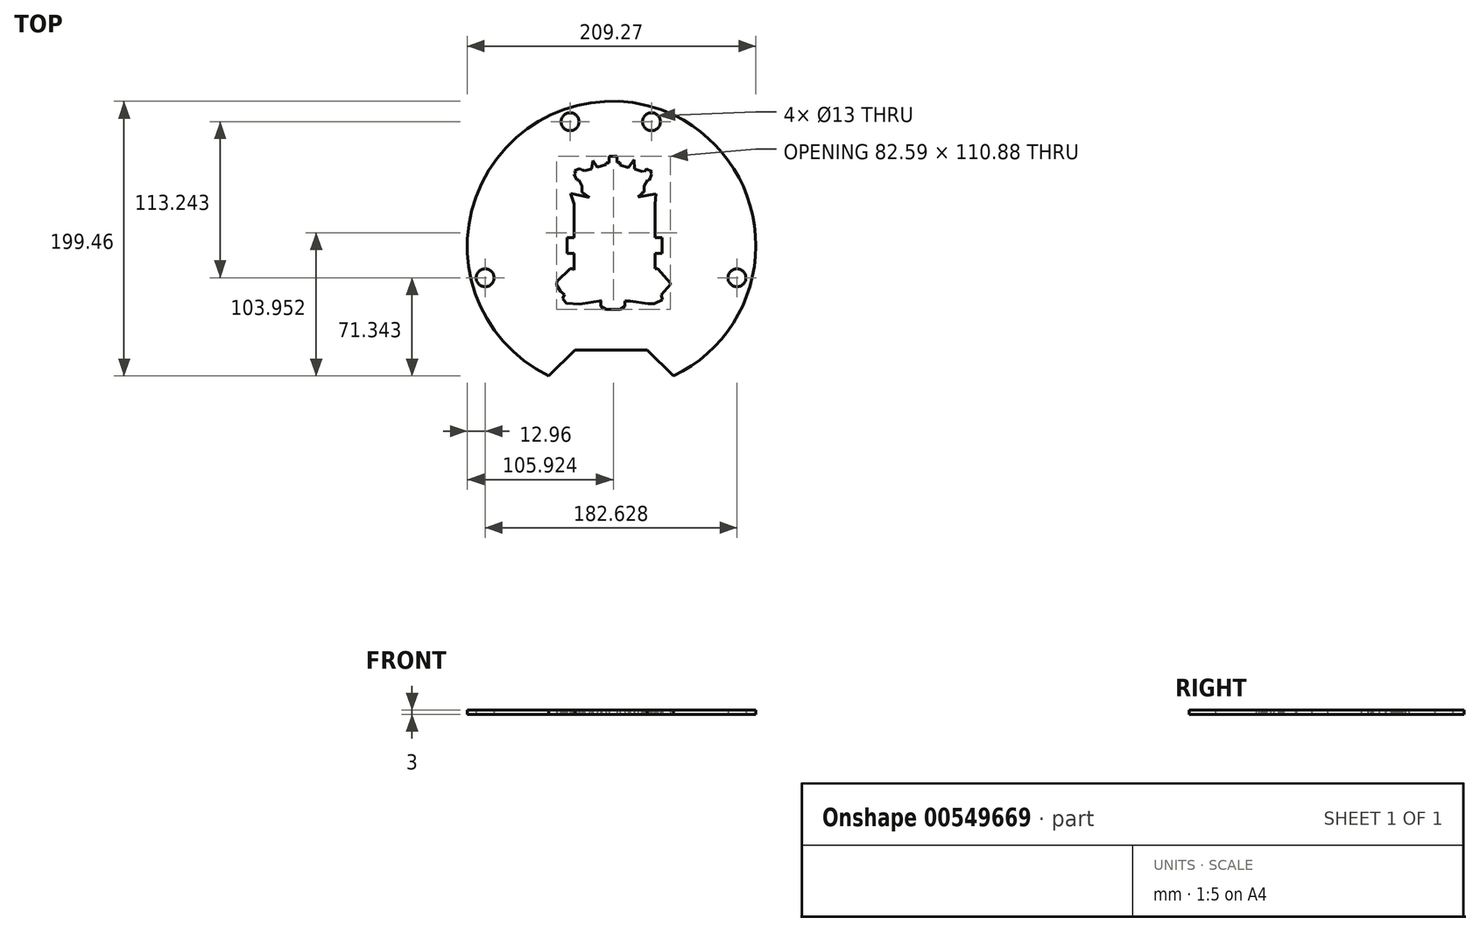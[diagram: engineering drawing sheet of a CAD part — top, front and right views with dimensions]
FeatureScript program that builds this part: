
annotation { "Feature Type Name" : "Feature", "Feature Type Description" : "" }
export const myFeature = defineFeature(function(context is Context, id is Id, definition is map)
    precondition{}
    {
        {
            var Q0;
            Q0=qCreatedBy(makeId("Top.planeOp"),FACE);
            var sketch = newSketch(context, id + "F0", { "sketchPlane" : qUnion([Q0])});
            skCircle(sketch, "E0", {"center": v(0, 0) * mm, "radius": 105 * mm});
            skLineSegment(sketch, "E1", {"start": v(0, 105) * mm, "end": v(0, -105) * mm});
            skLineSegment(sketch, "E2", {"start": v(0, 0) * mm, "end": v(0, 105) * mm});
            skLineSegment(sketch, "E3", {"start": v(-23.84, -72.43) * mm, "end": v(-45.86, -94.46) * mm});
            skLineSegment(sketch, "E4", {"start": v(22.77, -72.43) * mm, "end": v(45.13, -94.8) * mm});
            skPoint(sketch, "E5.firstSnap0", {"position": v(0, 46.64) * mm});
            skLineSegment(sketch, "E6", {"start": v(-21.81, 43.54) * mm, "end": v(-21.81, 39.03) * mm});
            skLineSegment(sketch, "E7", {"start": v(-21.81, 39.03) * mm, "end": v(-16.4, 35.15) * mm});
            skLineSegment(sketch, "E8", {"start": v(-16.4, 35.15) * mm, "end": v(-30.05, 38.05) * mm});
            skLineSegment(sketch, "E9", {"start": v(-30.05, 38.05) * mm, "end": v(-27.5, 30.4) * mm});
            skLineSegment(sketch, "E10", {"start": v(-27.5, 30.4) * mm, "end": v(-27.5, -17.4) * mm});
            skLineSegment(sketch, "E11", {"start": v(-27.5, -17.4) * mm, "end": v(-28.68, -16.54) * mm});
            skLineSegment(sketch, "E12", {"start": v(-28.68, -16.54) * mm, "end": v(-30.4, -16.54) * mm});
            skLineSegment(sketch, "E13", {"start": v(-30.4, -16.54) * mm, "end": v(-39.76, -25.66) * mm});
            skLineSegment(sketch, "E14", {"start": v(-39.76, -25.66) * mm, "end": v(-40.37, -28.38) * mm});
            skLineSegment(sketch, "E15", {"start": v(-40.37, -28.38) * mm, "end": v(-37.5, -32.94) * mm});
            skLineSegment(sketch, "E16", {"start": v(-37.5, -32.94) * mm, "end": v(-34.59, -35.38) * mm});
            skLineSegment(sketch, "E17", {"start": v(-34.59, -35.38) * mm, "end": v(-35.9, -38.1) * mm});
            skLineSegment(sketch, "E18", {"start": v(-35.9, -38.1) * mm, "end": v(-33.17, -41.48) * mm});
            skLineSegment(sketch, "E19", {"start": v(-33.17, -41.48) * mm, "end": v(-23.33, -42.39) * mm});
            skLineSegment(sketch, "E20", {"start": v(-23.33, -42.39) * mm, "end": v(-7.42, -39.66) * mm});
            skLineSegment(sketch, "E21", {"start": v(-7.42, -39.66) * mm, "end": v(-8.01, -40.48) * mm});
            skLineSegment(sketch, "E22", {"start": v(-8.01, -40.48) * mm, "end": v(-8.01, -43.95) * mm});
            skLineSegment(sketch, "E23", {"start": v(-8.01, -43.95) * mm, "end": v(-4.37, -45.95) * mm});
            skLineSegment(sketch, "E24", {"start": v(-4.37, -45.95) * mm, "end": v(5.8, -45.95) * mm});
            skLineSegment(sketch, "E25", {"start": v(5.8, -45.95) * mm, "end": v(9.28, -43.95) * mm});
            skLineSegment(sketch, "E26", {"start": v(9.28, -43.95) * mm, "end": v(9.28, -39.95) * mm});
            skLineSegment(sketch, "E27", {"start": v(9.28, -39.95) * mm, "end": v(12.99, -39.95) * mm});
            skLineSegment(sketch, "E28", {"start": v(12.99, -39.95) * mm, "end": v(26.17, -41.99) * mm});
            skLineSegment(sketch, "E29", {"start": v(26.17, -41.99) * mm, "end": v(30.42, -41.99) * mm});
            skLineSegment(sketch, "E30", {"start": v(30.42, -41.99) * mm, "end": v(36.63, -39.23) * mm});
            skLineSegment(sketch, "E31", {"start": v(36.63, -39.23) * mm, "end": v(35.61, -35.45) * mm});
            skLineSegment(sketch, "E32", {"start": v(35.61, -35.45) * mm, "end": v(42.22, -27.86) * mm});
            skLineSegment(sketch, "E33", {"start": v(42.22, -27.86) * mm, "end": v(42.22, -27.1) * mm});
            skLineSegment(sketch, "E34", {"start": v(42.22, -27.1) * mm, "end": v(33, -16.54) * mm});
            skLineSegment(sketch, "E35", {"start": v(33, -16.54) * mm, "end": v(31.3, -16.54) * mm});
            skLineSegment(sketch, "E36", {"start": v(31.3, -16.54) * mm, "end": v(31.3, -15.82) * mm});
            skLineSegment(sketch, "E37", {"start": v(31.3, 30.4) * mm, "end": v(31.9, 37.8) * mm});
            skLineSegment(sketch, "E38", {"start": v(31.9, 37.8) * mm, "end": v(18.8, 35.51) * mm});
            skLineSegment(sketch, "E39", {"start": v(18.8, 35.51) * mm, "end": v(21.27, 37.26) * mm});
            skLineSegment(sketch, "E40", {"start": v(21.27, 37.26) * mm, "end": v(21.27, 38.5) * mm});
            skLineSegment(sketch, "E41", {"start": v(21.27, 38.5) * mm, "end": v(23.37, 39.03) * mm});
            skLineSegment(sketch, "E42", {"start": v(23.37, 39.03) * mm, "end": v(23.37, 43.58) * mm});
            skLineSegment(sketch, "E43", {"start": v(23.37, 43.58) * mm, "end": v(25.7, 48.04) * mm});
            skLineSegment(sketch, "E44", {"start": v(25.7, 48.04) * mm, "end": v(27.02, 47.74) * mm});
            skLineSegment(sketch, "E45", {"start": v(27.02, 47.74) * mm, "end": v(28.71, 52) * mm});
            skLineSegment(sketch, "E46", {"start": v(28.71, 52) * mm, "end": v(27.66, 52.42) * mm});
            skLineSegment(sketch, "E47", {"start": v(27.66, 52.42) * mm, "end": v(28.82, 54.03) * mm});
            skLineSegment(sketch, "E48", {"start": v(28.82, 54.03) * mm, "end": v(24.86, 55.92) * mm});
            skLineSegment(sketch, "E49", {"start": v(24.86, 55.92) * mm, "end": v(23.5, 54.03) * mm});
            skLineSegment(sketch, "E50", {"start": v(23.5, 54.03) * mm, "end": v(22.53, 54.73) * mm});
            skLineSegment(sketch, "E51", {"start": v(22.53, 54.73) * mm, "end": v(22.03, 54.03) * mm});
            skLineSegment(sketch, "E52", {"start": v(22.03, 54.03) * mm, "end": v(16.25, 55.78) * mm});
            skLineSegment(sketch, "E53", {"start": v(16.25, 55.78) * mm, "end": v(15.85, 62.5) * mm});
            skLineSegment(sketch, "E54", {"start": v(15.85, 62.5) * mm, "end": v(11.81, 56.87) * mm});
            skLineSegment(sketch, "E55", {"start": v(11.81, 56.87) * mm, "end": v(5.72, 58.68) * mm});
            skLineSegment(sketch, "E56", {"start": v(5.72, 58.68) * mm, "end": v(5.72, 60.5) * mm});
            skLineSegment(sketch, "E57", {"start": v(5.72, 60.5) * mm, "end": v(3.69, 60.5) * mm});
            skLineSegment(sketch, "E58", {"start": v(3.69, 60.5) * mm, "end": v(3.69, 64.93) * mm});
            skLineSegment(sketch, "E59", {"start": v(3.69, 64.93) * mm, "end": v(-2.23, 64.93) * mm});
            skLineSegment(sketch, "E60", {"start": v(-2.23, 64.93) * mm, "end": v(-2.23, 60.24) * mm});
            skLineSegment(sketch, "E61", {"start": v(-2.23, 60.24) * mm, "end": v(-4.37, 60.24) * mm});
            skLineSegment(sketch, "E62", {"start": v(-4.37, 60.24) * mm, "end": v(-4.37, 58.9) * mm});
            skLineSegment(sketch, "E63", {"start": v(-4.37, 58.9) * mm, "end": v(-10.58, 57.27) * mm});
            skLineSegment(sketch, "E64", {"start": v(-10.58, 57.27) * mm, "end": v(-14.03, 61.99) * mm});
            skLineSegment(sketch, "E65", {"start": v(-14.03, 61.99) * mm, "end": v(-14.9, 55.78) * mm});
            skLineSegment(sketch, "E66", {"start": v(-14.9, 55.78) * mm, "end": v(-20, 54.44) * mm});
            skLineSegment(sketch, "E67", {"start": v(-20, 54.44) * mm, "end": v(-20.49, 54.79) * mm});
            skLineSegment(sketch, "E68", {"start": v(-20.49, 54.79) * mm, "end": v(-21.48, 54.79) * mm});
            skLineSegment(sketch, "E69", {"start": v(-21.48, 54.79) * mm, "end": v(-23.45, 56.2) * mm});
            skLineSegment(sketch, "E70", {"start": v(-23.45, 56.2) * mm, "end": v(-27.14, 54.44) * mm});
            skLineSegment(sketch, "E71", {"start": v(-27.14, 54.44) * mm, "end": v(-26.3, 52.66) * mm});
            skLineSegment(sketch, "E72", {"start": v(-26.3, 52.66) * mm, "end": v(-27.5, 52.09) * mm});
            skLineSegment(sketch, "E73", {"start": v(-27.5, 52.09) * mm, "end": v(-25.5, 47.91) * mm});
            skLineSegment(sketch, "E74", {"start": v(-25.5, 47.91) * mm, "end": v(-24.06, 47.91) * mm});
            skLineSegment(sketch, "E75", {"start": v(-24.06, 47.91) * mm, "end": v(-21.81, 43.54) * mm});
            skLineSegment(sketch, "E76", {"start": v(0.65, 37.6) * mm, "end": v(-3.56, 26.3) * mm});
            skLineSegment(sketch, "E77", {"start": v(-3.56, 26.3) * mm, "end": v(-16.92, 26.3) * mm});
            skLineSegment(sketch, "E78", {"start": v(-16.92, 26.3) * mm, "end": v(-6.29, 19.1) * mm});
            skLineSegment(sketch, "E79", {"start": v(-6.29, 19.1) * mm, "end": v(-11.32, 7.55) * mm});
            skLineSegment(sketch, "E80", {"start": v(-11.32, 7.55) * mm, "end": v(-8.64, 8.92) * mm});
            skLineSegment(sketch, "E81", {"start": v(-8.64, 8.92) * mm, "end": v(-9.73, 5.96) * mm});
            skLineSegment(sketch, "E82", {"start": v(-9.73, 5.96) * mm, "end": v(-25.24, 5.96) * mm});
            skLineSegment(sketch, "E83", {"start": v(-25.24, 5.96) * mm, "end": v(-25.24, 31.22) * mm});
            skLineSegment(sketch, "E84", {"start": v(-25.24, 31.22) * mm, "end": v(-27.14, 34.92) * mm});
            skLineSegment(sketch, "E85", {"start": v(-27.14, 34.92) * mm, "end": v(-19.74, 33.23) * mm});
            skLineSegment(sketch, "E86", {"start": v(-19.74, 33.23) * mm, "end": v(-11.27, 33.23) * mm});
            skLineSegment(sketch, "E87", {"start": v(-11.27, 33.23) * mm, "end": v(-4.33, 35.05) * mm});
            skLineSegment(sketch, "E88", {"start": v(-4.33, 35.05) * mm, "end": v(0.65, 37.6) * mm});
            skLineSegment(sketch, "E89", {"start": v(0.65, 37.6) * mm, "end": v(5.12, 35.23) * mm});
            skLineSegment(sketch, "E90", {"start": v(5.12, 35.23) * mm, "end": v(8.87, 33.83) * mm});
            skLineSegment(sketch, "E91", {"start": v(8.87, 33.83) * mm, "end": v(12.51, 32.97) * mm});
            skLineSegment(sketch, "E92", {"start": v(12.51, 32.97) * mm, "end": v(21.35, 32.97) * mm});
            skLineSegment(sketch, "E93", {"start": v(21.35, 32.97) * mm, "end": v(28.7, 35.43) * mm});
            skLineSegment(sketch, "E94", {"start": v(28.7, 35.43) * mm, "end": v(26.64, 31.22) * mm});
            skLineSegment(sketch, "E95", {"start": v(26.64, 31.22) * mm, "end": v(26.64, 5.96) * mm});
            skLineSegment(sketch, "E96", {"start": v(26.64, 5.96) * mm, "end": v(11.43, 5.96) * mm});
            skLineSegment(sketch, "E97", {"start": v(11.43, 5.96) * mm, "end": v(10.43, 8.92) * mm});
            skLineSegment(sketch, "E98", {"start": v(10.43, 8.92) * mm, "end": v(12.73, 7.33) * mm});
            skLineSegment(sketch, "E99", {"start": v(12.73, 7.33) * mm, "end": v(7.87, 19.24) * mm});
            skLineSegment(sketch, "E100", {"start": v(7.87, 19.24) * mm, "end": v(18.33, 26) * mm});
            skLineSegment(sketch, "E101", {"start": v(18.33, 26) * mm, "end": v(5.1, 26) * mm});
            skLineSegment(sketch, "E102", {"start": v(5.1, 26) * mm, "end": v(0.65, 37.6) * mm});
            skLineSegment(sketch, "E103", {"start": v(7.02, 11.06) * mm, "end": v(7.21, 5.96) * mm});
            skLineSegment(sketch, "E104", {"start": v(7.21, 5.96) * mm, "end": v(8.87, 5.96) * mm});
            skLineSegment(sketch, "E105", {"start": v(8.87, 5.96) * mm, "end": v(8.55, 9.92) * mm});
            skLineSegment(sketch, "E106", {"start": v(8.55, 9.92) * mm, "end": v(7.02, 11.06) * mm});
            skLineSegment(sketch, "E107", {"start": v(3.51, 13.32) * mm, "end": v(4.9, 12.5) * mm});
            skLineSegment(sketch, "E108", {"start": v(4.9, 12.5) * mm, "end": v(5.15, 5.96) * mm});
            skLineSegment(sketch, "E109", {"start": v(5.15, 5.96) * mm, "end": v(3.88, 5.9) * mm});
            skLineSegment(sketch, "E110", {"start": v(3.88, 5.9) * mm, "end": v(3.51, 13.32) * mm});
            skLineSegment(sketch, "E111", {"start": v(0.65, 14.8) * mm, "end": v(1.27, 14.57) * mm});
            skLineSegment(sketch, "E112", {"start": v(1.27, 14.57) * mm, "end": v(1.7, 5.96) * mm});
            skLineSegment(sketch, "E113", {"start": v(1.7, 5.96) * mm, "end": v(0.37, 5.9) * mm});
            skLineSegment(sketch, "E114", {"start": v(0.37, 5.9) * mm, "end": v(0.65, 14.8) * mm});
            skLineSegment(sketch, "E115", {"start": v(-2.37, 12.92) * mm, "end": v(-1.6, 13.32) * mm});
            skLineSegment(sketch, "E116", {"start": v(-1.6, 13.32) * mm, "end": v(-1.97, 5.96) * mm});
            skLineSegment(sketch, "E117", {"start": v(-1.97, 5.96) * mm, "end": v(-3.27, 6.02) * mm});
            skLineSegment(sketch, "E118", {"start": v(-3.27, 6.02) * mm, "end": v(-2.37, 12.92) * mm});
            skLineSegment(sketch, "E119", {"start": v(-5.96, 10.63) * mm, "end": v(-4.63, 11.31) * mm});
            skLineSegment(sketch, "E120", {"start": v(-4.63, 11.31) * mm, "end": v(-5.85, 5.96) * mm});
            skLineSegment(sketch, "E121", {"start": v(-5.85, 5.96) * mm, "end": v(-7.27, 5.96) * mm});
            skLineSegment(sketch, "E122", {"start": v(-7.27, 5.96) * mm, "end": v(-5.96, 10.63) * mm});
            skLineSegment(sketch, "E123", {"start": v(-25.33, -5.48) * mm, "end": v(-13.52, -5.48) * mm});
            skLineSegment(sketch, "E124", {"start": v(-13.52, -5.48) * mm, "end": v(-19.37, -24.28) * mm});
            skLineSegment(sketch, "E125", {"start": v(-19.37, -24.28) * mm, "end": v(-23.58, -20.79) * mm});
            skLineSegment(sketch, "E126", {"start": v(-23.58, -20.79) * mm, "end": v(-25.2, -17.64) * mm});
            skLineSegment(sketch, "E127", {"start": v(-25.2, -17.64) * mm, "end": v(-25.2, -14.31) * mm});
            skLineSegment(sketch, "E128", {"start": v(-25.2, -14.31) * mm, "end": v(-25.56, -13.61) * mm});
            skLineSegment(sketch, "E129", {"start": v(-25.56, -13.61) * mm, "end": v(-25.33, -5.48) * mm});
            skLineSegment(sketch, "E130", {"start": v(-10.13, -5.48) * mm, "end": v(-8.06, -5.4) * mm});
            skLineSegment(sketch, "E131", {"start": v(-8.06, -5.4) * mm, "end": v(-11.96, -24.86) * mm});
            skLineSegment(sketch, "E132", {"start": v(-11.96, -24.86) * mm, "end": v(-14.74, -24.97) * mm});
            skLineSegment(sketch, "E133", {"start": v(-14.74, -24.97) * mm, "end": v(-10.13, -5.48) * mm});
            skLineSegment(sketch, "E134", {"start": v(-4.78, -5.48) * mm, "end": v(-0.91, -5.34) * mm});
            skLineSegment(sketch, "E135", {"start": v(-0.91, -5.34) * mm, "end": v(-4.78, -26.64) * mm});
            skLineSegment(sketch, "E136", {"start": v(-4.78, -26.64) * mm, "end": v(-7.6, -25.61) * mm});
            skLineSegment(sketch, "E137", {"start": v(-7.6, -25.61) * mm, "end": v(-4.78, -5.48) * mm});
            skLineSegment(sketch, "E138", {"start": v(0, -5.48) * mm, "end": v(2.03, -5.4) * mm});
            skLineSegment(sketch, "E139", {"start": v(2.03, -5.4) * mm, "end": v(2.03, -29.34) * mm});
            skLineSegment(sketch, "E140", {"start": v(2.03, -29.34) * mm, "end": v(0.81, -30.9) * mm});
            skLineSegment(sketch, "E141", {"start": v(0.81, -30.9) * mm, "end": v(-0.37, -29.7) * mm});
            skLineSegment(sketch, "E142", {"start": v(-0.37, -29.7) * mm, "end": v(0, -5.48) * mm});
            skLineSegment(sketch, "E143", {"start": v(4.9, -5.48) * mm, "end": v(6.65, -5.48) * mm});
            skLineSegment(sketch, "E144", {"start": v(6.65, -5.48) * mm, "end": v(9.63, -25.94) * mm});
            skLineSegment(sketch, "E145", {"start": v(9.63, -25.94) * mm, "end": v(6.77, -26.35) * mm});
            skLineSegment(sketch, "E146", {"start": v(6.77, -26.35) * mm, "end": v(4.9, -5.48) * mm});
            skLineSegment(sketch, "E147", {"start": v(10.28, -5.48) * mm, "end": v(11.45, -5.48) * mm});
            skLineSegment(sketch, "E148", {"start": v(11.45, -5.48) * mm, "end": v(16.6, -24.85) * mm});
            skLineSegment(sketch, "E149", {"start": v(16.6, -24.85) * mm, "end": v(13.99, -24.85) * mm});
            skLineSegment(sketch, "E150", {"start": v(13.99, -24.85) * mm, "end": v(10.28, -5.48) * mm});
            skLineSegment(sketch, "E151", {"start": v(15.37, -5.48) * mm, "end": v(21.25, -23.9) * mm});
            skLineSegment(sketch, "E152", {"start": v(21.25, -23.9) * mm, "end": v(27.58, -19.89) * mm});
            skLineSegment(sketch, "E153", {"start": v(27.58, -19.89) * mm, "end": v(28.57, -17.17) * mm});
            skLineSegment(sketch, "E154", {"start": v(28.57, -17.17) * mm, "end": v(28.57, -5.34) * mm});
            skLineSegment(sketch, "E155", {"start": v(28.57, -5.34) * mm, "end": v(15.37, -5.48) * mm});
            skLineSegment(sketch, "E156", {"start": v(31.3, 30.4) * mm, "end": v(31.3, -15.82) * mm});
            skLineSegment(sketch, "E157", {"start": v(-27.5, 5.96) * mm, "end": v(-32.62, 5.96) * mm});
            skLineSegment(sketch, "E158", {"start": v(-32.62, 5.96) * mm, "end": v(-32.62, -5.48) * mm});
            skPoint(sketch, "E158.endSnap0", {"position": v(-19.42, -5.48) * mm});
            skLineSegment(sketch, "E159", {"start": v(-32.62, -5.48) * mm, "end": v(-27.5, -5.48) * mm});
            skLineSegment(sketch, "E160", {"start": v(-27.5, 5.96) * mm, "end": v(31.3, 5.96) * mm});
            skLineSegment(sketch, "E161", {"start": v(-27.5, -5.48) * mm, "end": v(31.3, -5.34) * mm});
            skLineSegment(sketch, "E162", {"start": v(31.3, -5.34) * mm, "end": v(36.42, -5.48) * mm});
            skLineSegment(sketch, "E163", {"start": v(31.3, 5.96) * mm, "end": v(36.42, 5.96) * mm});
            skLineSegment(sketch, "E164", {"start": v(36.42, 5.96) * mm, "end": v(36.42, -5.48) * mm});
            skCircle(sketch, "E165", {"center": v(-0.73, 0.35) * mm, "radius": 105 * mm});
            skCircle(sketch, "E166", {"center": v(-30.45, 90.13) * mm, "radius": 6.5 * mm});
            skCircle(sketch, "E167", {"center": v(28.57, 90.13) * mm, "radius": 6.5 * mm});
            skCircle(sketch, "E168", {"center": v(-92.04, -23.12) * mm, "radius": 6.5 * mm});
            skCircle(sketch, "E169", {"center": v(90.59, -23.12) * mm, "radius": 6.5 * mm});
            skLineSegment(sketch, "E170", {"start": v(-26.85, -75.44) * mm, "end": v(25.4, -75.44) * mm});
            skLineSegment(sketch, "E171", {"start": v(-26.85, -75.44) * mm, "end": v(-45.86, -94.46) * mm});
            skLineSegment(sketch, "E172", {"start": v(25.4, -75.44) * mm, "end": v(44.4, -94.46) * mm});
            skPoint(sketch, "E173.firstSnap0", {"position": v(-0.73, 52.63) * mm});
            skSolve(sketch);
        }
        {
            var Q0;
            Q0=makeQuery(id+"F0.imprint","IMPRINT",FACE,{"disambiguationData":[TD([[makeQuery(id+"F0.imprint","IMPRINT",EDGE,{"derivedFrom":sQuery(id+"F0.wireOp",EDGE,"E6")}),-1.0]])]});
            var Q1;
            {var subQ13=sQuery(id+"F0.wireOp",EDGE,"E25");Q1=makeQuery(id+"F0.imprint","IMPRINT",FACE,{"disambiguationData":[TD([[makeQuery(id+"F0.imprint","IMPRINT",EDGE,{"derivedFrom":subQ13}),-1.0]])]});}
            extrude(context, id + "F1", {"entities" : qUnion([Q0, Q1]), "depth" : 3 * mm, "offsetDistance" : 25.4 * mm});
        }
    });
